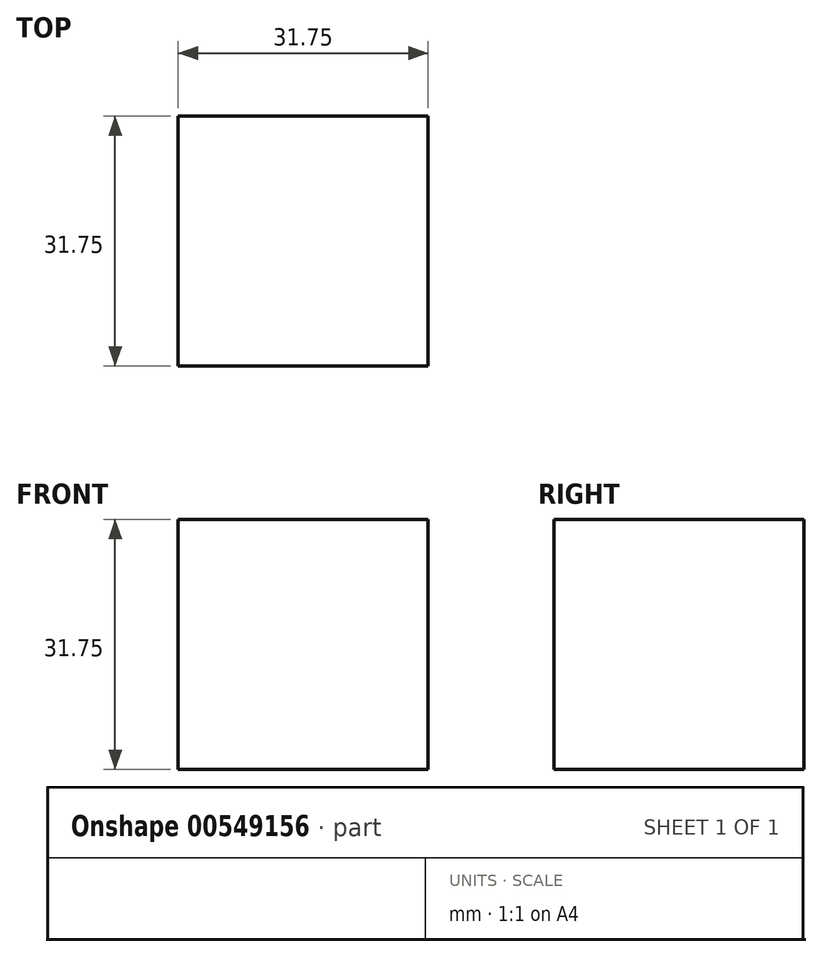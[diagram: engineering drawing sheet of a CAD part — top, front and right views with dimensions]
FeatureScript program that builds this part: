
annotation { "Feature Type Name" : "Feature", "Feature Type Description" : "" }
export const myFeature = defineFeature(function(context is Context, id is Id, definition is map)
    precondition{}
    {
        {
            var Q0;
            Q0=qCreatedBy(makeId("Front.planeOp"),FACE);
            var sketch = newSketch(context, id + "F0", { "sketchPlane" : qUnion([Q0])});
            skLineSegment(sketch, "E0", {"start": v(0, 0) * mm, "end": v(0, 31.75) * mm});
            skLineSegment(sketch, "E1", {"start": v(0, 31.75) * mm, "end": v(31.75, 31.75) * mm});
            skLineSegment(sketch, "E2", {"start": v(31.75, 31.75) * mm, "end": v(31.75, 0) * mm});
            skLineSegment(sketch, "E3", {"start": v(31.75, 0) * mm, "end": v(0, 0) * mm});
            skSolve(sketch);
        }
        {
            var Q0;
            Q0=makeQuery(id+"F0.imprint","IMPRINT",FACE,{"disambiguationData":[TD([[makeQuery(id+"F0.imprint","IMPRINT",EDGE,{"derivedFrom":sQuery(id+"F0.wireOp",EDGE,"E0")}),-1.0]])]});
            extrude(context, id + "F1", {"entities" : qUnion([Q0]), "depth" : 31.75 * mm, "offsetDistance" : 25.4 * mm});
        }
    });
